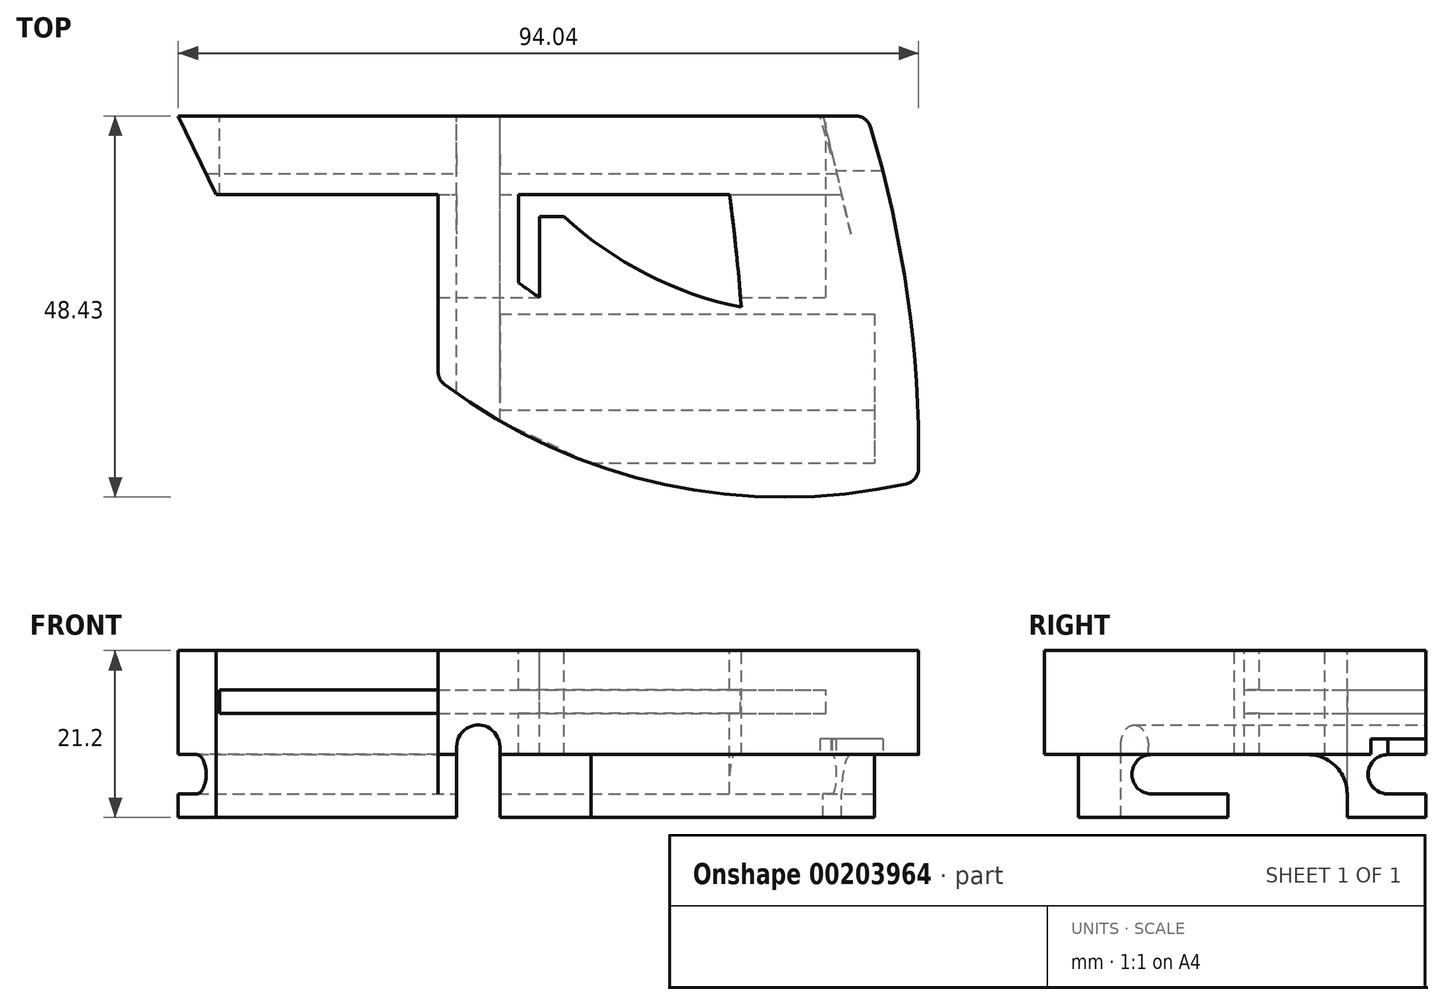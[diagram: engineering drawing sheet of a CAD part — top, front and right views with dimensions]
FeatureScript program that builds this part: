
annotation { "Feature Type Name" : "Feature", "Feature Type Description" : "" }
export const myFeature = defineFeature(function(context is Context, id is Id, definition is map)
    precondition{}
    {
        {
            var Q0;
            Q0=qCreatedBy(makeId("Top.planeOp"),FACE);
            var sketch = newSketch(context, id + "F0", { "sketchPlane" : qUnion([Q0])});
            skLineSegment(sketch, "E0", {"start": v(0, 0) * mm, "end": v(4.8, -10) * mm, "construction": true});
            skLineSegment(sketch, "E1", {"start": v(4.8, -10) * mm, "end": v(25, -10) * mm});
            skLineSegment(sketch, "E2", {"start": v(25, -10) * mm, "end": v(25, -33.5) * mm});
            skLineSegment(sketch, "E3", {"start": v(35.2, -10) * mm, "end": v(35.2, -40.06) * mm});
            skLineSegment(sketch, "E4", {"start": v(35.2, -10) * mm, "end": v(62, -10) * mm});
            skLineSegment(sketch, "E5", {"start": v(79.5, 0) * mm, "end": v(0, 0) * mm});
            skArc(sketch, "E6", {"start": v(86, -46.37) * mm, "mid": v(84.63, -22.92) * mm, "end": v(79.5, 0) * mm});
            skArc(sketch, "E7", {"start": v(25, -33.5) * mm, "mid": v(54.03, -46.88) * mm, "end": v(86, -46.37) * mm});
            skArc(sketch, "E8", {"start": v(63.93, -48.26) * mm, "mid": v(63.8, -29.09) * mm, "end": v(62, -10) * mm});
            skLineSegment(sketch, "E9", {"start": v(37.9, -27.55) * mm, "end": v(37.9, -12.8) * mm});
            skArc(sketch, "E10", {"start": v(41, -12.8) * mm, "mid": v(51.47, -20.1) * mm, "end": v(63.5, -24.3) * mm});
            skArc(sketch, "E11", {"start": v(37.9, -27.55) * mm, "mid": v(50.23, -34.84) * mm, "end": v(64.07, -38.5) * mm});
            skLineSegment(sketch, "E12", {"start": v(37.9, -12.8) * mm, "end": v(41, -12.8) * mm});
            skArc(sketch, "E13.0", {"start": v(35.2, -21.16) * mm, "mid": v(48.8, -28.7) * mm, "end": v(63.94, -32.2) * mm});
            skLineSegment(sketch, "E14", {"start": v(0, 0) * mm, "end": v(-8, 0) * mm});
            skLineSegment(sketch, "E15", {"start": v(-8, 0) * mm, "end": v(-3.2, -10) * mm});
            skLineSegment(sketch, "E16", {"start": v(-3.2, -10) * mm, "end": v(4.8, -10) * mm});
            skSolve(sketch);
        }
        {
            var Q0;
            Q0=makeQuery(id+"F0.imprint","IMPRINT",FACE,{"disambiguationData":[TD([[makeQuery(id+"F0.imprint","IMPRINT",EDGE,{"derivedFrom":sQuery(id+"F0.wireOp",EDGE,"E0")}),1.0]])]});
            var Q1;
            {var subQ0=sQuery(id+"F0.wireOp",EDGE,"E11");Q1=makeQuery(id+"F0.imprint","IMPRINT",FACE,{"disambiguationData":[TD([[makeQuery(id+"F0.imprint","IMPRINT",EDGE,{"derivedFrom":subQ0}),-1.0]])]});}
            var Q2;
            {var subQ1=sQuery(id+"F0.wireOp",EDGE,"E10");Q2=makeQuery(id+"F0.imprint","IMPRINT",FACE,{"disambiguationData":[TD([[makeQuery(id+"F0.imprint","IMPRINT",EDGE,{"derivedFrom":subQ1}),-1.0]])]});}
            var Q3;
            {var subQ0=sQuery(id+"F0.wireOp",EDGE,"E11");Q3=makeQuery(id+"F0.imprint","IMPRINT",FACE,{"disambiguationData":[TD([[makeQuery(id+"F0.imprint","IMPRINT",EDGE,{"derivedFrom":subQ0}),1.0]])]});}
            var Q4;
            Q4=makeQuery(id+"F0.imprint","IMPRINT",FACE,{"disambiguationData":[TD([[makeQuery(id+"F0.imprint","IMPRINT",EDGE,{"derivedFrom":sQuery(id+"F0.wireOp",EDGE,"E1")}),1.0]])]});
            extrude(context, id + "F1", {"entities" : qUnion([Q0, Q1, Q2, Q3, Q4]), "oppositeDirection" : true, "depth" : 13.2 * mm});
        }
        {
            var Q0;
            Q0=makeQuery(id+"F1.opExtrude","CAP_FACE",FACE,{"disambiguationData":[OSD([sQuery(id+"F0.wireOp",EDGE,"E0"),sQuery(id+"F0.wireOp",EDGE,"E1"),sQuery(id+"F0.wireOp",EDGE,"E2"),sQuery(id+"F0.wireOp",EDGE,"E3"),sQuery(id+"F0.wireOp",EDGE,"E4"),sQuery(id+"F0.wireOp",EDGE,"E5"),sQuery(id+"F0.wireOp",EDGE,"E6"),sQuery(id+"F0.wireOp",EDGE,"E7"),sQuery(id+"F0.wireOp",EDGE,"E8"),sQuery(id+"F0.wireOp",EDGE,"E9"),sQuery(id+"F0.wireOp",EDGE,"E10"),sQuery(id+"F0.wireOp",EDGE,"E12"),sQuery(id+"F0.wireOp",EDGE,"E13.0")])],"isStart":false});
            var sketch = newSketch(context, id + "F2", { "sketchPlane" : qUnion([Q0])});
            skLineSegment(sketch, "E17.0", {"start": v(25, 10) * mm, "end": v(25, 10) * mm});
            skLineSegment(sketch, "E18.0", {"start": v(27.35, 0) * mm, "end": v(0.35, 0) * mm});
            skLineSegment(sketch, "E19", {"start": v(25, 10) * mm, "end": v(27.35, 10) * mm});
            skLineSegment(sketch, "E20", {"start": v(27.35, 10) * mm, "end": v(27.35, 0) * mm});
            skPoint(sketch, "E21.orphan", {"position": v(79.5, 0) * mm});
            skLineSegment(sketch, "E22", {"start": v(73.9, 0) * mm, "end": v(76.26, 10) * mm});
            skLineSegment(sketch, "E23.0", {"start": v(35.2, 10) * mm, "end": v(62, 10) * mm});
            skLineSegment(sketch, "E24.0", {"start": v(73.9, 0) * mm, "end": v(32.85, 0) * mm});
            skLineSegment(sketch, "E25", {"start": v(62, 10) * mm, "end": v(76.26, 10) * mm});
            skLineSegment(sketch, "E26", {"start": v(35.2, 10) * mm, "end": v(32.85, 10) * mm});
            skLineSegment(sketch, "E27", {"start": v(32.85, 10) * mm, "end": v(32.85, 0) * mm});
            skLineSegment(sketch, "E28", {"start": v(80.44, 25.15) * mm, "end": v(80.44, 44.15) * mm});
            skLineSegment(sketch, "E29", {"start": v(80.44, 44.15) * mm, "end": v(44.44, 44.15) * mm});
            skLineSegment(sketch, "E30", {"start": v(44.44, 44.15) * mm, "end": v(32.85, 38.76) * mm});
            skLineSegment(sketch, "E31", {"start": v(32.85, 38.76) * mm, "end": v(32.85, 25.15) * mm});
            skLineSegment(sketch, "E32", {"start": v(80.44, 25.15) * mm, "end": v(32.85, 25.15) * mm});
            skLineSegment(sketch, "E33.0", {"start": v(-3.2, 10) * mm, "end": v(25, 10) * mm});
            skLineSegment(sketch, "E34.0", {"start": v(-8, 0) * mm, "end": v(-3.2, 10) * mm});
            skLineSegment(sketch, "E35.0", {"start": v(79.5, 0) * mm, "end": v(-8, 0) * mm});
            skLineSegment(sketch, "E36", {"start": v(25, 10) * mm, "end": v(35.2, 10) * mm, "construction": true});
            skLineSegment(sketch, "E37", {"start": v(30.1, 10) * mm, "end": v(30.1, 0) * mm, "construction": true});
            skSolve(sketch);
        }
        {
            var Q0;
            Q0 = qSketchRegion(id + "F2", true);
            extrude(context, id + "F3", {"entities" : qUnion([Q0]), "operationType" : NewBodyOperationType.ADD, "depth" : 8 * mm});
        }
        {
            var Q0;
            Q0=makeQuery(id+"F3.opExtrude","SWEPT_FACE",FACE,{"disambiguationData":[OSD([sQuery(id+"F2.wireOp",EDGE,"E28")])]});
            var sketch = newSketch(context, id + "F4", { "sketchPlane" : qUnion([Q0])});
            skLineSegment(sketch, "E38", {"start": v(0, -13.2) * mm, "end": v(-4.85, -13.2) * mm});
            skLineSegment(sketch, "E39", {"start": v(0, -18.2) * mm, "end": v(-4.85, -18.2) * mm});
            skArc(sketch, "E40", {"start": v(-4.85, -13.2) * mm, "mid": v(-7.35, -15.7) * mm, "end": v(-4.85, -18.2) * mm});
            skLineSegment(sketch, "E41", {"start": v(0, -13.2) * mm, "end": v(0, -18.2) * mm});
            skLineSegment(sketch, "E42.0", {"start": v(-10, -21.2) * mm, "end": v(-10, -18.2) * mm, "construction": true});
            skLineSegment(sketch, "E43.1.0.0", {"start": v(-30, -18.2) * mm, "end": v(-34.85, -18.2) * mm});
            skArc(sketch, "E43.1.0.1", {"start": v(-34.85, -13.2) * mm, "mid": v(-37.35, -15.7) * mm, "end": v(-34.85, -18.2) * mm});
            skLineSegment(sketch, "E43.1.0.2", {"start": v(-30, -13.2) * mm, "end": v(-34.85, -13.2) * mm});
            skLineSegment(sketch, "E43.direction1", {"start": v(-4.85, -18.2) * mm, "end": v(-34.85, -18.2) * mm, "construction": true});
            skPoint(sketch, "E44.orphan", {"position": v(-10, -13.2) * mm});
            skLineSegment(sketch, "E45", {"start": v(-30, -18.2) * mm, "end": v(-25.15, -18.2) * mm});
            skLineSegment(sketch, "E46", {"start": v(-25.15, -18.2) * mm, "end": v(-25.15, -13.2) * mm});
            skLineSegment(sketch, "E47", {"start": v(-25.15, -13.2) * mm, "end": v(-30, -13.2) * mm});
            skSolve(sketch);
        }
        {
            var Q0;
            Q0 = qSketchRegion(id + "F4", true);
            extrude(context, id + "F5", {"entities" : qUnion([Q0]), "operationType" : NewBodyOperationType.REMOVE, "endBound" : BoundingType.THROUGH_ALL, "oppositeDirection" : true, "depth" : 25 * mm});
        }
        {
            var Q0;
            {var subQ0=sQuery(id+"F0.wireOp",EDGE,"E6");var subQ7=sQuery(id+"F0.wireOp",EDGE,"E5");Q0=makeQuery(id+"F5.boolean.opBoolean","SPLIT",FACE,{"disambiguationData":[TD([makeQuery(id+"F1.opExtrude","SWEPT_FACE",FACE,{"disambiguationData":[OSD([subQ0])]})])],"derivedFrom":makeQuery(id+"F3.boolean.opBoolean","MERGE",FACE,{"derivedFrom":[makeQuery(id+"F1.opExtrude","SWEPT_FACE",FACE,{"disambiguationData":[OSD([subQ7])]}),makeQuery(id+"F3.opExtrude","SWEPT_FACE",FACE,{"disambiguationData":[OSD([sQuery(id+"F2.wireOp",EDGE,"E24.0")])]}),makeQuery(id+"F3.opExtrude","SWEPT_FACE",FACE,{"disambiguationData":[OSD([sQuery(id+"F2.wireOp",EDGE,"E18.0")])]})]})});}
            var sketch = newSketch(context, id + "F6", { "sketchPlane" : qUnion([Q0])});
            skLineSegment(sketch, "E48.0", {"start": v(-32.85, -18.2) * mm, "end": v(-32.85, -13.2) * mm, "construction": true});
            skLineSegment(sketch, "E49", {"start": v(-27.35, -13.2) * mm, "end": v(-32.85, -13.2) * mm});
            skLineSegment(sketch, "E50", {"start": v(-27.35, -13.2) * mm, "end": v(-27.35, -12.2) * mm});
            skLineSegment(sketch, "E51", {"start": v(-32.85, -13.2) * mm, "end": v(-32.85, -12.2) * mm});
            skArc(sketch, "E52", {"start": v(-27.35, -12.2) * mm, "mid": v(-30.1, -9.45) * mm, "end": v(-32.85, -12.2) * mm});
            skLineSegment(sketch, "E53.bottom", {"start": v(2.75, -8) * mm, "end": v(-74.25, -8) * mm});
            skLineSegment(sketch, "E53.top", {"start": v(2.75, -5) * mm, "end": v(-74.25, -5) * mm});
            skLineSegment(sketch, "E53.left", {"start": v(2.75, -8) * mm, "end": v(2.75, -5) * mm});
            skLineSegment(sketch, "E53.right", {"start": v(-74.25, -8) * mm, "end": v(-74.25, -5) * mm});
            skLineSegment(sketch, "E54.0", {"start": v(-79.5, 0) * mm, "end": v(-79.5, 0) * mm});
            skLineSegment(sketch, "E55", {"start": v(-35.75, 0) * mm, "end": v(-35.75, -27.7) * mm, "construction": true});
            skPoint(sketch, "E56.0", {"position": v(-27.35, -18.2) * mm});
            skLineSegment(sketch, "E57", {"start": v(-27.35, -18.2) * mm, "end": v(-27.35, -13.2) * mm, "construction": true});
            skSolve(sketch);
        }
        {
            var Q0;
            Q0=makeQuery(id+"F6.imprint","IMPRINT",FACE,{"disambiguationData":[TD([[makeQuery(id+"F6.imprint","IMPRINT",EDGE,{"derivedFrom":sQuery(id+"F6.wireOp",EDGE,"E49")}),1.0]])]});
            extrude(context, id + "F7", {"entities" : qUnion([Q0]), "operationType" : NewBodyOperationType.REMOVE, "endBound" : BoundingType.THROUGH_ALL, "oppositeDirection" : true, "depth" : 25 * mm});
        }
        {
            var Q0;
            Q0=makeQuery(id+"F6.imprint","IMPRINT",FACE,{"disambiguationData":[TD([[makeQuery(id+"F6.imprint","IMPRINT",EDGE,{"derivedFrom":sQuery(id+"F6.wireOp",EDGE,"E53.bottom")}),-1.0]])]});
            var Q1;
            Q1=makeQuery(id+"F1.opExtrude","SWEPT_FACE",FACE,{"disambiguationData":[OSD([sQuery(id+"F0.wireOp",EDGE,"E12")])]});
            extrude(context, id + "F8", {"entities" : qUnion([Q0]), "operationType" : NewBodyOperationType.REMOVE, "endBound" : BoundingType.UP_TO_SURFACE, "oppositeDirection" : true, "endBoundEntityFace" : qUnion([Q1]), "depth" : 25 * mm});
        }
        {
            var Q0;
            {var subQ0=sQuery(id+"F0.wireOp",EDGE,"E8");var subQ2=sQuery(id+"F2.wireOp",EDGE,"E26");var subQ3=sQuery(id+"F2.wireOp",EDGE,"E25");var subQ4=sQuery(id+"F2.wireOp",EDGE,"E23.0");Q0=makeQuery(id+"F3.boolean.opBoolean","SPLIT",EDGE,{"disambiguationData":[TD([makeQuery(id+"F1.opExtrude","SWEPT_FACE",FACE,{"disambiguationData":[OSD([subQ0])]})])],"derivedFrom":makeQuery(id+"F3.opExtrude","CAP_EDGE",EDGE,{"disambiguationData":[OSD([subQ4,subQ3,subQ2])],"isStart":true})});}
            var Q1;
            Q1=makeQuery(id+"F3.opExtrude","CAP_EDGE",EDGE,{"disambiguationData":[OSD([sQuery(id+"F2.wireOp",EDGE,"E17.0"),sQuery(id+"F2.wireOp",EDGE,"E19")])],"isStart":true});
            fillet(context, id + "F9", {"entities" : qUnion([Q0, Q1]), "radius" : 5 * mm, "tangentPropagation" : true, "allowEdgeOverflow" : false});
        }
        {
            var Q0;
            Q0=makeQuery(id+"F1.opExtrude","SWEPT_EDGE",EDGE,{"disambiguationData":[OSD([sQuery(id+"F0.wireOp",EDGE,"E6"),sQuery(id+"F0.wireOp",EDGE,"E7")])]});
            var Q1;
            Q1=makeQuery(id+"F1.opExtrude","SWEPT_EDGE",EDGE,{"disambiguationData":[OSD([sQuery(id+"F0.wireOp",EDGE,"E5"),sQuery(id+"F0.wireOp",EDGE,"E6")])]});
            var Q2;
            Q2=makeQuery(id+"F1.opExtrude","SWEPT_EDGE",EDGE,{"disambiguationData":[OSD([sQuery(id+"F0.wireOp",EDGE,"E2"),sQuery(id+"F0.wireOp",EDGE,"E7")])]});
            var Q3;
            {var subQ0=sQuery(id+"F0.wireOp",EDGE,"E5");var subQ1=sQuery(id+"F2.wireOp",EDGE,"d6eed3e1-1f6e-4b8a-b15b-9e3aff0553e7.0");var subQ13=sQuery(id+"F0.wireOp",EDGE,"E0");var subQ14=sQuery(id+"F2.wireOp",EDGE,"E18.0");Q3=makeQuery(id+"F5.boolean.opBoolean","SPLIT",EDGE,{"disambiguationData":[TD([makeQuery(id+"F5.opExtrude","SWEPT_FACE",FACE,{"disambiguationData":[OSD([sQuery(id+"F4.wireOp",EDGE,"E38")])]})])],"derivedFrom":makeQuery(id+"F3.boolean.opBoolean","MERGE",EDGE,{"derivedFrom":[makeQuery(id+"F1.opExtrude","SWEPT_EDGE",EDGE,{"disambiguationData":[OSD([subQ13,subQ0])]}),makeQuery(id+"F3.opExtrude","SWEPT_EDGE",EDGE,{"disambiguationData":[OSD([subQ1,subQ14])]})]})});}
            var Q4;
            {var subQ0=sQuery(id+"F0.wireOp",EDGE,"E5");var subQ1=sQuery(id+"F2.wireOp",EDGE,"d6eed3e1-1f6e-4b8a-b15b-9e3aff0553e7.0");var subQ2=sQuery(id+"F2.wireOp",EDGE,"E18.0");var subQ3=sQuery(id+"F0.wireOp",EDGE,"E0");Q4=makeQuery(id+"F5.boolean.opBoolean","SPLIT",EDGE,{"disambiguationData":[TD([makeQuery(id+"F5.opExtrude","SWEPT_FACE",FACE,{"disambiguationData":[OSD([sQuery(id+"F4.wireOp",EDGE,"E39")])]})])],"derivedFrom":makeQuery(id+"F3.boolean.opBoolean","MERGE",EDGE,{"derivedFrom":[makeQuery(id+"F1.opExtrude","SWEPT_EDGE",EDGE,{"disambiguationData":[OSD([subQ3,subQ0])]}),makeQuery(id+"F3.opExtrude","SWEPT_EDGE",EDGE,{"disambiguationData":[OSD([subQ1,subQ2])]})]})});}
            fillet(context, id + "F10", {"entities" : qUnion([Q0, Q1, Q2, Q3, Q4]), "radius" : 2 * mm, "tangentPropagation" : true, "allowEdgeOverflow" : false});
        }
        {
            var Q0;
            {var subQ0=makeQuery(id+"F3.opExtrude","SWEPT_FACE",FACE,{"disambiguationData":[OSD([sQuery(id+"F2.wireOp",EDGE,"E18.0")])]});var subQ1=sQuery(id+"F0.wireOp",EDGE,"E5");var subQ2=makeQuery(id+"F1.opExtrude","SWEPT_FACE",FACE,{"disambiguationData":[OSD([subQ1])]});var subQ3=makeQuery(id+"F3.opExtrude","SWEPT_FACE",FACE,{"disambiguationData":[OSD([sQuery(id+"F2.wireOp",EDGE,"E30")])]});var subQ4=sQuery(id+"F0.wireOp",EDGE,"E10");var subQ5=makeQuery(id+"F1.opExtrude","SWEPT_FACE",FACE,{"disambiguationData":[OSD([subQ4])]});var subQ6=makeQuery(id+"F3.opExtrude","SWEPT_FACE",FACE,{"disambiguationData":[OSD([sQuery(id+"F2.wireOp",EDGE,"E28")])]});var subQ7=sQuery(id+"F0.wireOp",EDGE,"E9");var subQ8=makeQuery(id+"F1.opExtrude","SWEPT_FACE",FACE,{"disambiguationData":[OSD([subQ7])]});var subQ9=makeQuery(id+"F3.opExtrude","SWEPT_FACE",FACE,{"disambiguationData":[OSD([sQuery(id+"F2.wireOp",EDGE,"E23.0"),sQuery(id+"F2.wireOp",EDGE,"E25"),sQuery(id+"F2.wireOp",EDGE,"E26")])]});var subQ10=makeQuery(id+"F5.opExtrude","SWEPT_FACE",FACE,{"disambiguationData":[OSD([sQuery(id+"F4.wireOp",EDGE,"E38")])]});var subQ11=makeQuery(id+"F5.opExtrude","SWEPT_FACE",FACE,{"disambiguationData":[OSD([sQuery(id+"F4.wireOp",EDGE,"E43.1.0.2")])]});var subQ12=makeQuery(id+"F3.opExtrude","SWEPT_FACE",FACE,{"disambiguationData":[OSD([sQuery(id+"F2.wireOp",EDGE,"E27")])]});var subQ13=sQuery(id+"F0.wireOp",EDGE,"E13.0");var subQ14=sQuery(id+"F0.wireOp",EDGE,"E12");var subQ15=sQuery(id+"F0.wireOp",EDGE,"E8");var subQ16=sQuery(id+"F0.wireOp",EDGE,"E7");var subQ17=sQuery(id+"F0.wireOp",EDGE,"E6");var subQ18=sQuery(id+"F0.wireOp",EDGE,"E4");var subQ19=sQuery(id+"F0.wireOp",EDGE,"E3");var subQ20=sQuery(id+"F0.wireOp",EDGE,"E2");var subQ21=sQuery(id+"F0.wireOp",EDGE,"E1");var subQ22=makeQuery(id+"F1.opExtrude","CAP_FACE",FACE,{"disambiguationData":[OSD([sQuery(id+"F0.wireOp",EDGE,"E0"),subQ21,subQ20,subQ19,subQ18,subQ1,subQ17,subQ16,subQ15,subQ7,subQ4,subQ14,subQ13])],"isStart":false});var subQ23=makeQuery(id+"F3.opExtrude","SWEPT_FACE",FACE,{"disambiguationData":[OSD([sQuery(id+"F2.wireOp",EDGE,"E22")])]});var subQ24=makeQuery(id+"F3.opExtrude","SWEPT_FACE",FACE,{"disambiguationData":[OSD([sQuery(id+"F2.wireOp",EDGE,"E24.0")])]});var subQ25=makeQuery(id+"F1.opExtrude","SWEPT_FACE",FACE,{"disambiguationData":[OSD([subQ13])]});var subQ26=makeQuery(id+"F3.opExtrude","SWEPT_FACE",FACE,{"disambiguationData":[OSD([sQuery(id+"F2.wireOp",EDGE,"E31")])]});var subQ27=makeQuery(id+"F1.opExtrude","SWEPT_FACE",FACE,{"disambiguationData":[OSD([subQ18])]});var subQ28=makeQuery(id+"F1.opExtrude","SWEPT_FACE",FACE,{"disambiguationData":[OSD([subQ19])]});var subQ29=makeQuery(id+"F1.opExtrude","SWEPT_FACE",FACE,{"disambiguationData":[OSD([subQ14])]});var subQ30=makeQuery(id+"F3.opExtrude","SWEPT_FACE",FACE,{"disambiguationData":[OSD([sQuery(id+"F2.wireOp",EDGE,"E29")])]});var subQ31=makeQuery(id+"F1.opExtrude","SWEPT_FACE",FACE,{"disambiguationData":[OSD([subQ17])]});var subQ32=makeQuery(id+"F1.opExtrude","SWEPT_FACE",FACE,{"disambiguationData":[OSD([subQ16])]});var subQ33=makeQuery(id+"F1.opExtrude","SWEPT_FACE",FACE,{"disambiguationData":[OSD([subQ15])]});var subQ34=makeQuery(id+"F3.opExtrude","SWEPT_FACE",FACE,{"disambiguationData":[OSD([sQuery(id+"F2.wireOp",EDGE,"Ljg5KV3S-6eCn-r9bq-Nvar-5ImZNwAfBAfD")])]});Q0=makeQuery(id+"F7.boolean.opBoolean","SPLIT",FACE,{"disambiguationData":[TD([subQ28])],"derivedFrom":makeQuery(id+"F5.boolean.opBoolean","MERGE",FACE,{"derivedFrom":[makeQuery(id+"F3.boolean.opBoolean","SPLIT",FACE,{"disambiguationData":[TD([subQ22,makeQuery(id+"F1.opExtrude","SWEPT_FACE",FACE,{"disambiguationData":[OSD([subQ21])]}),makeQuery(id+"F1.opExtrude","SWEPT_FACE",FACE,{"disambiguationData":[OSD([subQ20])]}),subQ28,subQ27,subQ2,subQ32,subQ33,subQ8,subQ5,subQ29,subQ25,makeQuery(id+"F3.opExtrude","SWEPT_FACE",FACE,{"disambiguationData":[OSD([sQuery(id+"F2.wireOp",EDGE,"E17.0"),sQuery(id+"F2.wireOp",EDGE,"E19")])]}),makeQuery(id+"F3.opExtrude","SWEPT_FACE",FACE,{"disambiguationData":[OSD([sQuery(id+"F2.wireOp",EDGE,"E20")])]}),subQ9,subQ24,subQ12,subQ0,subQ34,subQ3,subQ26])],"derivedFrom":subQ22}),makeQuery(id+"F3.boolean.opBoolean","SPLIT",FACE,{"disambiguationData":[TD([subQ22,subQ27,subQ2,subQ31,subQ32,subQ33,subQ5,subQ23,subQ9,subQ24,subQ0,subQ34,subQ6,subQ30,subQ3])],"derivedFrom":subQ22}),subQ10,subQ11]})});}
            var sketch = newSketch(context, id + "F11", { "sketchPlane" : qUnion([Q0])});
            skLineSegment(sketch, "E58.0", {"start": v(78.02, 0) * mm, "end": v(32.85, 0) * mm});
            skArc(sketch, "E59.0", {"start": v(78.02, 0) * mm, "mid": v(79.21, 0.4) * mm, "end": v(79.94, 1.43) * mm});
            skArc(sketch, "E60.0", {"start": v(86.03, 44.8) * mm, "mid": v(84.63, 22.88) * mm, "end": v(79.94, 1.43) * mm});
            skLineSegment(sketch, "E61", {"start": v(81.49, 7) * mm, "end": v(75.55, 7) * mm});
            skLineSegment(sketch, "E62", {"start": v(75.55, 7) * mm, "end": v(73.49, 0) * mm});
            skSolve(sketch);
        }
        {
            var Q0;
            {var subQ1=sQuery(id+"F11.wireOp",EDGE,"E59.0");Q0=makeQuery(id+"F11.imprint","IMPRINT",FACE,{"disambiguationData":[TD([[makeQuery(id+"F11.imprint","IMPRINT",EDGE,{"derivedFrom":subQ1}),1.0]])]});}
            extrude(context, id + "F12", {"entities" : qUnion([Q0]), "operationType" : NewBodyOperationType.REMOVE, "oppositeDirection" : true, "depth" : 2 * mm});
        }
        {
            var Q0;
            {var subQ0=sQuery(id+"F0.wireOp",EDGE,"E6");var subQ3=sQuery(id+"F0.wireOp",EDGE,"E14");var subQ10=sQuery(id+"F0.wireOp",EDGE,"E5");var subQ15=sQuery(id+"F2.wireOp",EDGE,"E34.0");var subQ16=sQuery(id+"F2.wireOp",EDGE,"E35.0");Q0=makeQuery(id+"F5.boolean.opBoolean","SPLIT",FACE,{"disambiguationData":[TD([makeQuery(id+"F1.opExtrude","SWEPT_FACE",FACE,{"disambiguationData":[OSD([subQ0])]})])],"derivedFrom":makeQuery(id+"F3.boolean.opBoolean","MERGE",FACE,{"derivedFrom":[makeQuery(id+"F1.opExtrude","SWEPT_FACE",FACE,{"disambiguationData":[OSD([subQ10,subQ3])]}),makeQuery(id+"F3.opExtrude","SWEPT_FACE",FACE,{"disambiguationData":[OSD([subQ16]),TDD([makeQuery(id+"F2.imprint","IMPRINT",EDGE,{"disambiguationData":[TD([[makeQuery(id+"F2.imprint","INTERSECT",VERTEX,{"derivedFrom":[sQuery(id+"F2.wireOp",EDGE,"E22"),subQ16]}),-1.0]])],"derivedFrom":subQ16})])]}),makeQuery(id+"F3.opExtrude","SWEPT_FACE",FACE,{"disambiguationData":[OSD([subQ16]),TDD([makeQuery(id+"F2.imprint","IMPRINT",EDGE,{"disambiguationData":[TD([[makeQuery(id+"F2.imprint","INTERSECT",VERTEX,{"derivedFrom":[subQ15,subQ16]}),1.0]])],"derivedFrom":subQ16})])]})]})});}
            var sketch = newSketch(context, id + "F13", { "sketchPlane" : qUnion([Q0])});
            skLineSegment(sketch, "E63.0", {"start": v(2.75, -8) * mm, "end": v(-37.9, -8) * mm});
            skLineSegment(sketch, "E64.0", {"start": v(2.75, -8) * mm, "end": v(2.75, -5) * mm});
            skLineSegment(sketch, "E65.0", {"start": v(2.75, -5) * mm, "end": v(-37.9, -5) * mm});
            skLineSegment(sketch, "E66.0", {"start": v(-74.25, -8) * mm, "end": v(-74.25, -5) * mm});
            skLineSegment(sketch, "E67.0", {"start": v(-37.9, -8) * mm, "end": v(-37.9, -5) * mm});
            skPoint(sketch, "E68.orphan", {"position": v(-37.9, -13.2) * mm});
            skPoint(sketch, "E69.orphan", {"position": v(-37.9, 0) * mm});
            skLineSegment(sketch, "E70.trimOffspring", {"start": v(-62, -5) * mm, "end": v(-74.25, -5) * mm});
            skLineSegment(sketch, "E71.trimOffspring", {"start": v(-62, -8) * mm, "end": v(-74.25, -8) * mm});
            skPoint(sketch, "E72.orphan", {"position": v(-63.5, -13.2) * mm});
            skPoint(sketch, "E73.orphan", {"position": v(-63.5, 0) * mm});
            skLineSegment(sketch, "E74.0", {"start": v(-62, -5) * mm, "end": v(-62, 0) * mm, "construction": true});
            skLineSegment(sketch, "E75", {"start": v(-62, -5) * mm, "end": v(-62, -8) * mm});
            skSolve(sketch);
        }
        {
            var Q0;
            Q0 = qSketchRegion(id + "F13", true);
            var Q1;
            Q1=makeQuery(id+"F1.opExtrude","CAP_VERTEX",VERTEX,{"disambiguationData":[OSD([sQuery(id+"F0.wireOp",EDGE,"E9"),sQuery(id+"F0.wireOp",EDGE,"E13.0")])],"isStart":true});
            extrude(context, id + "F14", {"entities" : qUnion([Q0]), "operationType" : NewBodyOperationType.REMOVE, "endBound" : BoundingType.UP_TO_VERTEX, "oppositeDirection" : true, "endBoundEntityVertex" : qUnion([Q1]), "depth" : 25 * mm});
        }
    });
